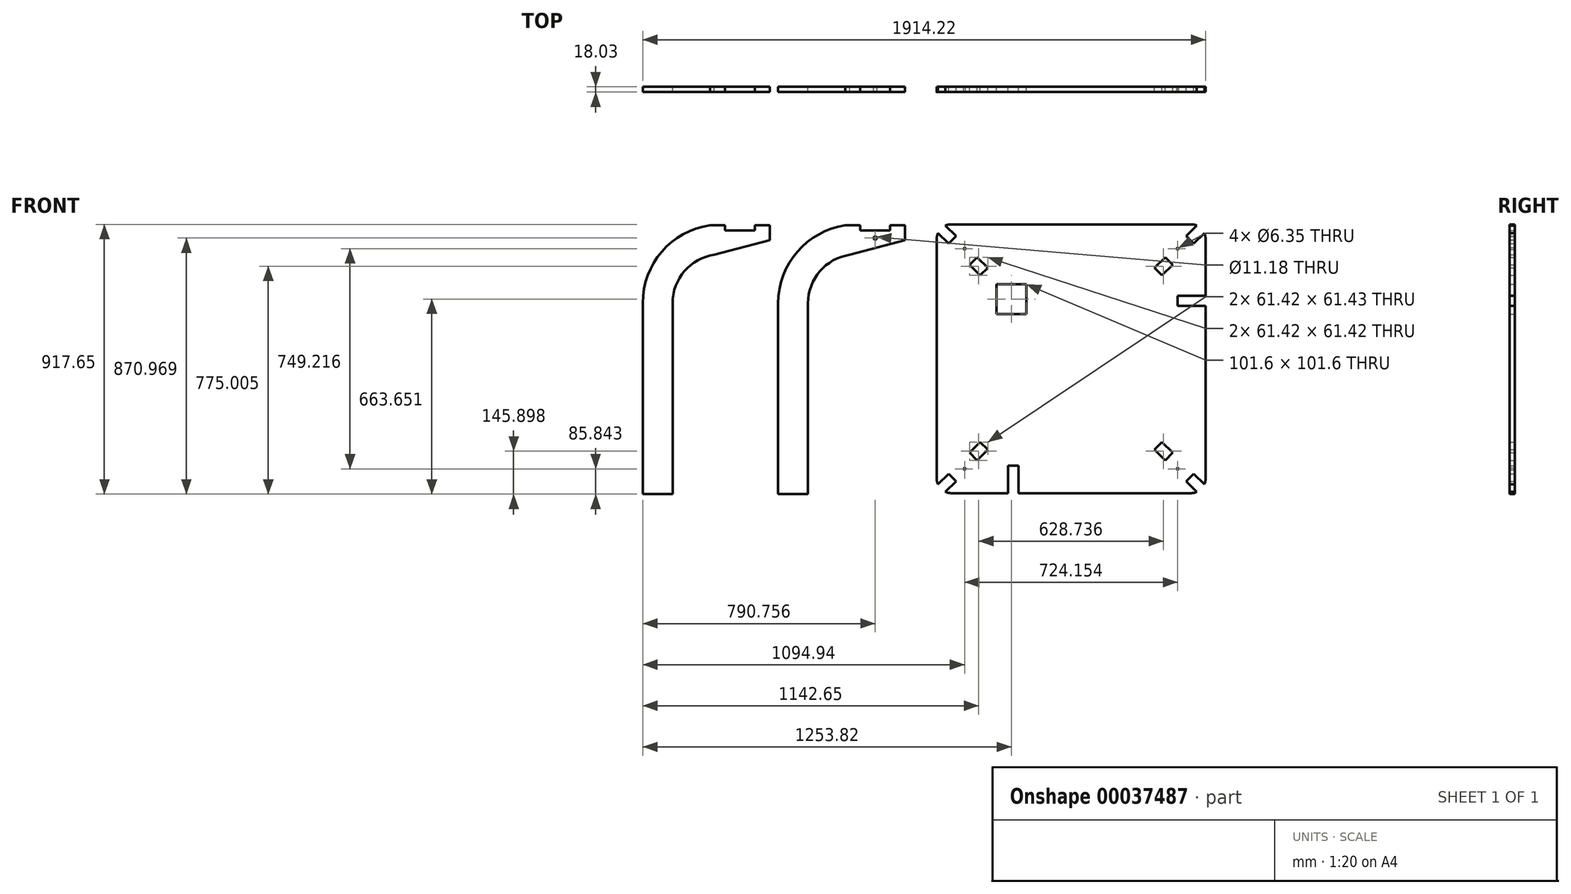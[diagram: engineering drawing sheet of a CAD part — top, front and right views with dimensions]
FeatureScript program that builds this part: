
annotation { "Feature Type Name" : "Feature", "Feature Type Description" : "" }
export const myFeature = defineFeature(function(context is Context, id is Id, definition is map)
    precondition{}
    {
        {
            var Q0;
            Q0=qCreatedBy(makeId("Front.planeOp"),FACE);
            var sketch = newSketch(context, id + "F0", { "sketchPlane" : qUnion([Q0])});
            skLineSegment(sketch, "E0", {"start": v(432.4, 424.67) * mm, "end": v(483.2, 424.67) * mm});
            skLineSegment(sketch, "E1", {"start": v(483.2, 424.67) * mm, "end": v(483.2, 406.64) * mm});
            skLineSegment(sketch, "E2", {"start": v(483.2, 406.64) * mm, "end": v(584.8, 406.64) * mm});
            skLineSegment(sketch, "E3", {"start": v(635.6, 406.64) * mm, "end": v(635.6, 341.1) * mm, "construction": true});
            skLineSegment(sketch, "E4.bottom", {"start": v(792.88, 427.92) * mm, "end": v(1607.65, 427.92) * mm});
            skLineSegment(sketch, "E4.top", {"start": v(792.88, -486.48) * mm, "end": v(986.23, -486.48) * mm});
            skLineSegment(sketch, "E4.left", {"start": v(743.07, 378.1) * mm, "end": v(743.07, -436.67) * mm});
            skLineSegment(sketch, "E4.right", {"start": v(1657.47, 378.1) * mm, "end": v(1657.47, 185.08) * mm});
            skArc(sketch, "E5.filletArc", {"start": v(792.88, 427.92) * mm, "mid": v(782.69, 426.87) * mm, "end": v(772.93, 423.75) * mm});
            skLineSegment(sketch, "E6", {"start": v(757.75, 413.43) * mm, "end": v(795.96, 375.01) * mm, "construction": true});
            skLineSegment(sketch, "E7", {"start": v(795.96, 375.01) * mm, "end": v(808.74, 387.73) * mm});
            skLineSegment(sketch, "E8", {"start": v(808.74, 387.73) * mm, "end": v(772.93, 423.75) * mm});
            skLineSegment(sketch, "E9.MirrorCS", {"start": v(795.96, 375.01) * mm, "end": v(783.17, 362.3) * mm});
            skLineSegment(sketch, "E10.MirrorCS", {"start": v(783.17, 362.3) * mm, "end": v(747.35, 398.32) * mm});
            skLineSegment(sketch, "E11", {"start": v(1200.27, 427.92) * mm, "end": v(1200.27, -486.48) * mm, "construction": true});
            skLineSegment(sketch, "E12", {"start": v(1657.47, -29.28) * mm, "end": v(743.07, -29.28) * mm, "construction": true});
            skArc(sketch, "E13.trimOffspring", {"start": v(747.35, 398.32) * mm, "mid": v(744.15, 388.44) * mm, "end": v(743.07, 378.1) * mm});
            skLineSegment(sketch, "E14", {"start": v(534, 375.65) * mm, "end": v(534, 406.64) * mm, "construction": true});
            skPoint(sketch, "E14.startSnap0", {"position": v(534, 394.27) * mm});
            skCircle(sketch, "E15", {"center": v(534, 381.24) * mm, "radius": 5.59 * mm});
            skLineSegment(sketch, "E16", {"start": v(203.8, -489.73) * mm, "end": v(305.4, -489.73) * mm});
            skLineSegment(sketch, "E17", {"start": v(432.4, 374.35) * mm, "end": v(635.6, 374.35) * mm, "construction": true});
            skPoint(sketch, "E17.endSnap0", {"position": v(635.6, 373.87) * mm});
            skLineSegment(sketch, "E18", {"start": v(534, 374.35) * mm, "end": v(534, 391.41) * mm, "construction": true});
            skLineSegment(sketch, "E19.MirrorCS", {"start": v(584.8, 424.67) * mm, "end": v(584.8, 406.64) * mm});
            skLineSegment(sketch, "E20.MirrorCS", {"start": v(635.6, 424.67) * mm, "end": v(584.8, 424.67) * mm});
            skLineSegment(sketch, "E21", {"start": v(635.6, 424.67) * mm, "end": v(635.6, 406.64) * mm});
            skLineSegment(sketch, "E22.MirrorCS", {"start": v(855.18, 290.48) * mm, "end": v(891.1, 254.56) * mm});
            skLineSegment(sketch, "E23.MirrorCS", {"start": v(880.69, 315.99) * mm, "end": v(916.6, 280.07) * mm});
            skLineSegment(sketch, "E24", {"start": v(916.6, 280.07) * mm, "end": v(891.1, 254.56) * mm});
            skLineSegment(sketch, "E25.bottom", {"start": v(946.27, 224.72) * mm, "end": v(1047.87, 224.72) * mm});
            skLineSegment(sketch, "E25.top", {"start": v(946.27, 123.12) * mm, "end": v(1047.87, 123.12) * mm});
            skLineSegment(sketch, "E25.left", {"start": v(946.27, 224.72) * mm, "end": v(946.27, 123.12) * mm});
            skLineSegment(sketch, "E25.right", {"start": v(1047.87, 224.72) * mm, "end": v(1047.87, 123.12) * mm});
            skLineSegment(sketch, "E26.right", {"start": v(986.23, -488.02) * mm, "end": v(986.23, -392.77) * mm});
            skLineSegment(sketch, "E27.bottom", {"start": v(986.23, -392.77) * mm, "end": v(1021.16, -392.77) * mm});
            skLineSegment(sketch, "E27.right", {"start": v(1021.16, -392.77) * mm, "end": v(1021.16, -486.48) * mm});
            skLineSegment(sketch, "E28.trimOffspring", {"start": v(1021.16, -486.48) * mm, "end": v(1607.65, -486.48) * mm});
            skLineSegment(sketch, "E29.MirrorCS", {"start": v(1657.47, 185.08) * mm, "end": v(1562.22, 185.08) * mm});
            skLineSegment(sketch, "E30.MirrorCS", {"start": v(1562.22, 185.08) * mm, "end": v(1562.22, 150.16) * mm});
            skLineSegment(sketch, "E31.MirrorCS", {"start": v(1562.22, 150.16) * mm, "end": v(1657.47, 150.16) * mm});
            skLineSegment(sketch, "E32.trimOffspring", {"start": v(1657.47, 150.16) * mm, "end": v(1657.47, -436.67) * mm});
            skLineSegment(sketch, "E33", {"start": v(635.6, 406.64) * mm, "end": v(635.6, 373.87) * mm});
            skLineSegment(sketch, "E34", {"start": v(802.35, 381.37) * mm, "end": v(874.03, 309.29) * mm, "construction": true});
            skLineSegment(sketch, "E35", {"start": v(831.8, 338.96) * mm, "end": v(838.19, 345.33) * mm, "construction": true});
            skCircle(sketch, "E36", {"center": v(838.19, 345.33) * mm, "radius": 3.18 * mm});
            skLineSegment(sketch, "E37", {"start": v(880.69, 315.99) * mm, "end": v(855.18, 290.48) * mm});
            skLineSegment(sketch, "E38.MirrorCS", {"start": v(1604.57, 375.01) * mm, "end": v(1617.36, 362.3) * mm});
            skLineSegment(sketch, "E39.MirrorCS", {"start": v(1604.57, 375.01) * mm, "end": v(1591.79, 387.73) * mm});
            skLineSegment(sketch, "E40.MirrorCS", {"start": v(1568.73, 338.96) * mm, "end": v(1562.34, 345.33) * mm});
            skCircle(sketch, "E41.MirrorC", {"center": v(1562.34, 345.33) * mm, "radius": 3.18 * mm});
            skLineSegment(sketch, "E42.MirrorCS", {"start": v(1483.92, 280.07) * mm, "end": v(1509.42, 254.56) * mm});
            skArc(sketch, "E43.MirrorCS", {"start": v(1653.18, 398.32) * mm, "mid": v(1656.38, 388.44) * mm, "end": v(1657.47, 378.1) * mm});
            skLineSegment(sketch, "E44.MirrorCS", {"start": v(1519.84, 315.99) * mm, "end": v(1545.35, 290.48) * mm});
            skArc(sketch, "E45.MirrorCS", {"start": v(1607.65, 427.92) * mm, "mid": v(1617.84, 426.87) * mm, "end": v(1627.6, 423.75) * mm});
            skLineSegment(sketch, "E46.MirrorCS", {"start": v(1519.84, 315.99) * mm, "end": v(1483.92, 280.07) * mm});
            skLineSegment(sketch, "E47.MirrorCS", {"start": v(1617.36, 362.3) * mm, "end": v(1653.18, 398.32) * mm});
            skLineSegment(sketch, "E48.MirrorCS", {"start": v(1591.79, 387.73) * mm, "end": v(1627.6, 423.75) * mm});
            skLineSegment(sketch, "E49.MirrorCS", {"start": v(1545.35, 290.48) * mm, "end": v(1509.42, 254.56) * mm});
            skLineSegment(sketch, "E50.MirrorCS", {"start": v(1598.18, 381.37) * mm, "end": v(1526.5, 309.29) * mm});
            skLineSegment(sketch, "E51.MirrorCS", {"start": v(1642.78, 413.43) * mm, "end": v(1604.57, 375.01) * mm});
            skCircle(sketch, "E52.MirrorC", {"center": v(838.19, -403.89) * mm, "radius": 3.18 * mm});
            skLineSegment(sketch, "E53.MirrorCS", {"start": v(831.8, -397.52) * mm, "end": v(838.19, -403.89) * mm});
            skArc(sketch, "E54.MirrorCS", {"start": v(792.88, -486.48) * mm, "mid": v(782.69, -485.42) * mm, "end": v(772.93, -482.3) * mm});
            skArc(sketch, "E55.MirrorCS", {"start": v(747.35, -456.88) * mm, "mid": v(744.15, -447) * mm, "end": v(743.07, -436.67) * mm});
            skLineSegment(sketch, "E56.MirrorCS", {"start": v(795.96, -433.57) * mm, "end": v(808.74, -446.29) * mm});
            skLineSegment(sketch, "E57.MirrorCS", {"start": v(795.96, -433.57) * mm, "end": v(783.17, -420.85) * mm});
            skLineSegment(sketch, "E58.MirrorCS", {"start": v(808.74, -446.29) * mm, "end": v(772.93, -482.3) * mm});
            skLineSegment(sketch, "E59.MirrorCS", {"start": v(757.75, -471.99) * mm, "end": v(795.96, -433.57) * mm});
            skLineSegment(sketch, "E60.MirrorCS", {"start": v(855.18, -349.04) * mm, "end": v(891.1, -313.12) * mm});
            skLineSegment(sketch, "E61.MirrorCS", {"start": v(880.69, -374.54) * mm, "end": v(916.6, -338.62) * mm});
            skLineSegment(sketch, "E62.MirrorCS", {"start": v(783.17, -420.85) * mm, "end": v(747.35, -456.88) * mm});
            skLineSegment(sketch, "E63.MirrorCS", {"start": v(916.6, -338.62) * mm, "end": v(891.1, -313.12) * mm});
            skLineSegment(sketch, "E64.MirrorCS", {"start": v(880.69, -374.54) * mm, "end": v(855.18, -349.04) * mm});
            skLineSegment(sketch, "E65.MirrorCS", {"start": v(802.35, -439.93) * mm, "end": v(874.03, -367.85) * mm});
            skLineSegment(sketch, "E66.MirrorCS", {"start": v(1604.57, -433.57) * mm, "end": v(1591.79, -446.29) * mm});
            skLineSegment(sketch, "E67.MirrorCS", {"start": v(1604.57, -433.57) * mm, "end": v(1617.36, -420.85) * mm});
            skArc(sketch, "E68.MirrorCS", {"start": v(1653.18, -456.88) * mm, "mid": v(1656.38, -447) * mm, "end": v(1657.47, -436.67) * mm});
            skLineSegment(sketch, "E69.MirrorCS", {"start": v(1568.73, -397.52) * mm, "end": v(1562.34, -403.89) * mm});
            skLineSegment(sketch, "E70.MirrorCS", {"start": v(1483.92, -338.62) * mm, "end": v(1509.42, -313.12) * mm});
            skLineSegment(sketch, "E71.MirrorCS", {"start": v(1519.84, -374.54) * mm, "end": v(1545.35, -349.04) * mm});
            skCircle(sketch, "E72.MirrorC", {"center": v(1562.34, -403.89) * mm, "radius": 3.18 * mm});
            skArc(sketch, "E73.MirrorCS", {"start": v(1607.65, -486.48) * mm, "mid": v(1617.84, -485.42) * mm, "end": v(1627.6, -482.3) * mm});
            skLineSegment(sketch, "E74.MirrorCS", {"start": v(1598.18, -439.93) * mm, "end": v(1526.5, -367.85) * mm});
            skLineSegment(sketch, "E75.MirrorCS", {"start": v(1617.36, -420.85) * mm, "end": v(1653.18, -456.88) * mm});
            skLineSegment(sketch, "E76.MirrorCS", {"start": v(1519.84, -374.54) * mm, "end": v(1483.92, -338.62) * mm});
            skLineSegment(sketch, "E77.MirrorCS", {"start": v(1591.79, -446.29) * mm, "end": v(1627.6, -482.3) * mm});
            skLineSegment(sketch, "E78.MirrorCS", {"start": v(1642.78, -471.99) * mm, "end": v(1604.57, -433.57) * mm});
            skLineSegment(sketch, "E79.MirrorCS", {"start": v(1545.35, -349.04) * mm, "end": v(1509.42, -313.12) * mm});
            skLineSegment(sketch, "E80", {"start": v(305.4, -489.73) * mm, "end": v(305.4, 159.52) * mm});
            skLineSegment(sketch, "E81", {"start": v(203.8, -489.73) * mm, "end": v(203.8, 159.52) * mm});
            skArc(sketch, "E82", {"start": v(432.4, 424.67) * mm, "mid": v(268.85, 334.56) * mm, "end": v(203.8, 159.52) * mm});
            skArc(sketch, "E83.0", {"start": v(447.37, 324.18) * mm, "mid": v(345.8, 268.22) * mm, "end": v(305.4, 159.52) * mm});
            skLineSegment(sketch, "E84", {"start": v(447.37, 324.18) * mm, "end": v(635.6, 374.35) * mm});
            skPoint(sketch, "E85.endSnap0", {"position": v(175.05, 374.22) * mm});
            skLineSegment(sketch, "E86", {"start": v(-256.75, -489.38) * mm, "end": v(-256.75, 159.86) * mm});
            skLineSegment(sketch, "E87", {"start": v(-13.2, 324.52) * mm, "end": v(175.05, 374.69) * mm});
            skLineSegment(sketch, "E88", {"start": v(-256.75, -489.38) * mm, "end": v(-155.15, -489.38) * mm});
            skArc(sketch, "E89.0", {"start": v(-13.2, 324.52) * mm, "mid": v(-114.76, 268.56) * mm, "end": v(-155.15, 159.86) * mm});
            skLineSegment(sketch, "E90", {"start": v(-155.15, -489.38) * mm, "end": v(-155.15, 159.86) * mm});
            skArc(sketch, "E91", {"start": v(-28.15, 425.02) * mm, "mid": v(-191.71, 334.9) * mm, "end": v(-256.75, 159.86) * mm});
            skLineSegment(sketch, "E85", {"start": v(-28.15, 374.69) * mm, "end": v(175.05, 374.69) * mm, "construction": true});
            skLineSegment(sketch, "E92", {"start": v(175.05, 406.98) * mm, "end": v(175.05, 341.45) * mm, "construction": true});
            skLineSegment(sketch, "E93", {"start": v(-28.15, 425.02) * mm, "end": v(22.65, 425.02) * mm});
            skLineSegment(sketch, "E94", {"start": v(175.05, 406.98) * mm, "end": v(175.05, 374.22) * mm});
            skLineSegment(sketch, "E95", {"start": v(22.65, 406.98) * mm, "end": v(124.25, 406.98) * mm});
            skLineSegment(sketch, "E96", {"start": v(175.05, 425.02) * mm, "end": v(175.05, 406.98) * mm});
            skLineSegment(sketch, "E97.MirrorCS", {"start": v(175.05, 425.02) * mm, "end": v(124.25, 425.02) * mm});
            skLineSegment(sketch, "E98", {"start": v(22.65, 425.02) * mm, "end": v(22.65, 406.98) * mm});
            skLineSegment(sketch, "E99.MirrorCS", {"start": v(124.25, 425.02) * mm, "end": v(124.25, 406.98) * mm});
            skPoint(sketch, "E100.endSnap0", {"position": v(-205.95, -489.38) * mm});
            skSolve(sketch);
        }
        {
            var Q0;
            Q0=makeQuery(id+"F0.imprint","IMPRINT",FACE,{"disambiguationData":[TD([[makeQuery(id+"F0.imprint","IMPRINT",EDGE,{"derivedFrom":sQuery(id+"F0.wireOp",EDGE,"E0")}),-1.0]])]});
            var Q1;
            Q1=makeQuery(id+"F0.imprint","IMPRINT",FACE,{"disambiguationData":[TD([[makeQuery(id+"F0.imprint","IMPRINT",EDGE,{"derivedFrom":sQuery(id+"F0.wireOp",EDGE,"E4.bottom")}),-1.0]])]});
            var Q2;
            Q2=makeQuery(id+"F0.imprint","IMPRINT",FACE,{"disambiguationData":[TD([[makeQuery(id+"F0.imprint","IMPRINT",EDGE,{"derivedFrom":sQuery(id+"F0.wireOp",EDGE,"52b04602-891c-4f0b-9f4b-30c39f058121")}),1.0]])]});
            var Q3;
            Q3=makeQuery(id+"F0.imprint","IMPRINT",FACE,{"disambiguationData":[TD([[makeQuery(id+"F0.imprint","IMPRINT",EDGE,{"derivedFrom":sQuery(id+"F0.wireOp",EDGE,"e6eb8baf-ef0b-4c92-a250-6a5ced1377bc")}),1.0]])]});
            var Q4;
            Q4=makeQuery(id+"F0.imprint","IMPRINT",FACE,{"disambiguationData":[TD([[makeQuery(id+"F0.imprint","IMPRINT",EDGE,{"derivedFrom":sQuery(id+"F0.wireOp",EDGE,"E86")}),-1.0]])]});
            extrude(context, id + "F1", {"entities" : qUnion([Q0, Q1, Q2, Q3, Q4]), "offsetDistance" : 25.4 * mm, "depth" : 18.03 * mm});
        }
    });
